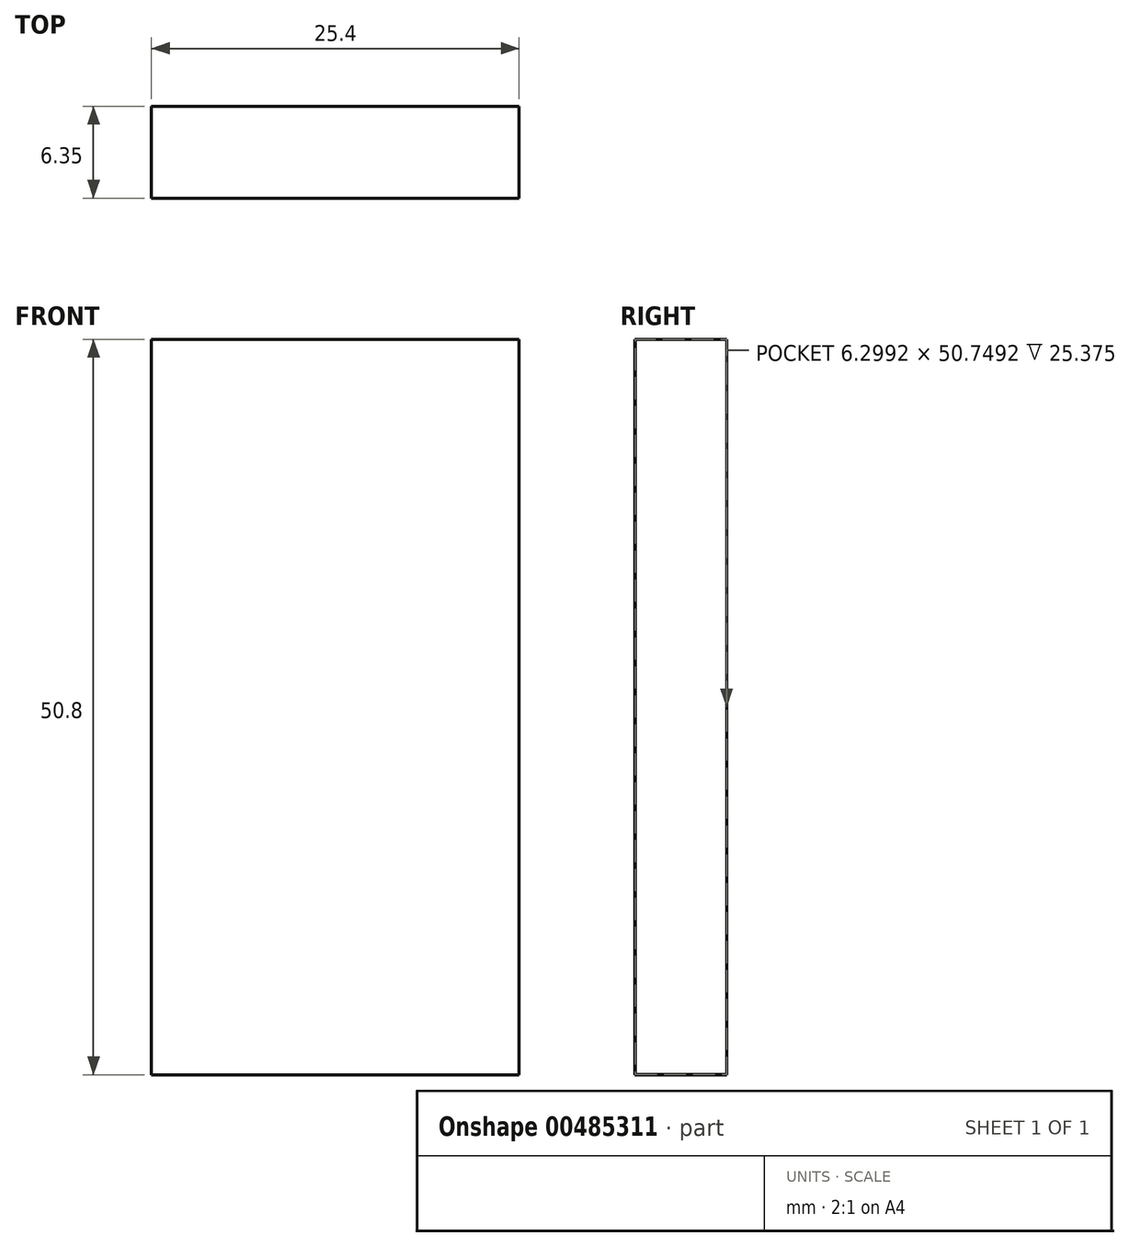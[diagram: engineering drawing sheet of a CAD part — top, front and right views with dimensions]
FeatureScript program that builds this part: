
annotation { "Feature Type Name" : "Feature", "Feature Type Description" : "" }
export const myFeature = defineFeature(function(context is Context, id is Id, definition is map)
    precondition{}
    {
        {
            var Q0;
            Q0=qCreatedBy(makeId("Top.planeOp"),FACE);
            var sketch = newSketch(context, id + "F0", { "sketchPlane" : qUnion([Q0])});
            skLineSegment(sketch, "E0.bottom", {"start": v(-304.8, 190.5) * mm, "end": v(304.8, 190.5) * mm});
            skLineSegment(sketch, "E0.top", {"start": v(-304.8, -190.5) * mm, "end": v(304.8, -190.5) * mm});
            skLineSegment(sketch, "E0.left", {"start": v(-304.8, 190.5) * mm, "end": v(-304.8, -190.5) * mm});
            skLineSegment(sketch, "E0.right", {"start": v(304.8, 190.5) * mm, "end": v(304.8, -190.5) * mm});
            skPoint(sketch, "E0.middle", {"position": v(0, 0) * mm});
            skSolve(sketch);
        }
        {
            var Q0;
            Q0=makeQuery(id+"F0.imprint","IMPRINT",FACE,{"disambiguationData":[TD([[makeQuery(id+"F0.imprint","IMPRINT",EDGE,{"derivedFrom":sQuery(id+"F0.wireOp",EDGE,"E0.bottom")}),-1.0]])]});
            extrude(context, id + "F1", {"entities" : qUnion([Q0]), "depth" : 19.05 * mm});
        }
        {
            var Q0;
            Q0=makeQuery(id+"F1.opExtrude","CAP_EDGE",EDGE,{"disambiguationData":[OSD([sQuery(id+"F0.wireOp",EDGE,"E0.top")])],"isStart":true});
            var Q1;
            Q1=makeQuery(id+"F1.opExtrude","CAP_EDGE",EDGE,{"disambiguationData":[OSD([sQuery(id+"F0.wireOp",EDGE,"E0.right")])],"isStart":true});
            var Q2;
            Q2=makeQuery(id+"F1.opExtrude","CAP_EDGE",EDGE,{"disambiguationData":[OSD([sQuery(id+"F0.wireOp",EDGE,"E0.bottom")])],"isStart":true});
            var Q3;
            Q3=makeQuery(id+"F1.opExtrude","CAP_EDGE",EDGE,{"disambiguationData":[OSD([sQuery(id+"F0.wireOp",EDGE,"E0.left")])],"isStart":true});
            chamfer(context, id + "F2", {"entities" : qUnion([Q0, Q1, Q2, Q3]), "chamferType" : ChamferType.OFFSET_ANGLE, "width" : 12.7 * mm, "oppositeDirection" : false, "angle" : 65 * degree, "tangentPropagation" : true});
        }
        {
            var Q0;
            Q0=qCreatedBy(makeId("Right.planeOp"),FACE);
            var sketch = newSketch(context, id + "F3", { "sketchPlane" : qUnion([Q0])});
            skLineSegment(sketch, "E1.bottom", {"start": v(-25.4, 444.5) * mm, "end": v(25.4, 444.5) * mm});
            skLineSegment(sketch, "E1.top", {"start": v(-25.4, -444.5) * mm, "end": v(25.4, -444.5) * mm});
            skLineSegment(sketch, "E1.left", {"start": v(-25.4, 444.5) * mm, "end": v(-25.4, -444.5) * mm});
            skLineSegment(sketch, "E1.right", {"start": v(25.4, 444.5) * mm, "end": v(25.4, -444.5) * mm});
            skPoint(sketch, "E1.middle", {"position": v(0, 0) * mm});
            skSolve(sketch);
        }
        {
            var Q0;
            Q0 = qSketchRegion(id + "F3", true);
            extrude(context, id + "F4", {"entities" : qUnion([Q0]), "endBound" : BoundingType.SYMMETRIC, "depth" : 50.8 * mm});
        }
        {
            var Q0;
            Q0=makeQuery(id+"F4.opExtrude","CAP_FACE",FACE,{"disambiguationData":[OSD([sQuery(id+"F3.wireOp",EDGE,"E1.bottom"),sQuery(id+"F3.wireOp",EDGE,"E1.top"),sQuery(id+"F3.wireOp",EDGE,"E1.left"),sQuery(id+"F3.wireOp",EDGE,"E1.right")])],"isStart":false});
            var sketch = newSketch(context, id + "F5", { "sketchPlane" : qUnion([Q0])});
            skLineSegment(sketch, "E2.bottom", {"start": v(12.7, 431.8) * mm, "end": v(6.35, 431.8) * mm});
            skLineSegment(sketch, "E2.top", {"start": v(12.7, 381) * mm, "end": v(6.35, 381) * mm});
            skLineSegment(sketch, "E2.left", {"start": v(12.7, 431.8) * mm, "end": v(12.7, 381) * mm});
            skLineSegment(sketch, "E2.right", {"start": v(6.35, 431.8) * mm, "end": v(6.35, 381) * mm});
            skSolve(sketch);
        }
        {
            var Q0;
            Q0=makeQuery(id+"F5.imprint","IMPRINT",FACE,{"disambiguationData":[TD([[makeQuery(id+"F5.imprint","IMPRINT",EDGE,{"derivedFrom":sQuery(id+"F5.wireOp",EDGE,"E2.bottom")}),1.0]])]});
            extrude(context, id + "F6", {"entities" : qUnion([Q0]), "operationType" : NewBodyOperationType.INTERSECT, "depth" : -25.4 * mm});
        }
        {
            var Q0;
            Q0=makeQuery(id+"F4.opExtrude","CAP_FACE",FACE,{"disambiguationData":[OSD([sQuery(id+"F3.wireOp",EDGE,"E1.bottom"),sQuery(id+"F3.wireOp",EDGE,"E1.top"),sQuery(id+"F3.wireOp",EDGE,"E1.left"),sQuery(id+"F3.wireOp",EDGE,"E1.right")])],"isStart":false});
            var Q1;
            Q1=makeQuery(id+"F4.opExtrude","SWEPT_BODY",BODY,{"disambiguationData":[OSD([sQuery(id+"F3.wireOp",EDGE,"E1.bottom"),sQuery(id+"F3.wireOp",EDGE,"E1.top"),sQuery(id+"F3.wireOp",EDGE,"E1.left"),sQuery(id+"F3.wireOp",EDGE,"E1.right")])]});
            shell(context, id + "F7", {"entities" : qUnion([Q0]), "parts" : qUnion([Q1]), "thickness" : 0.03 * mm});
        }
    });
